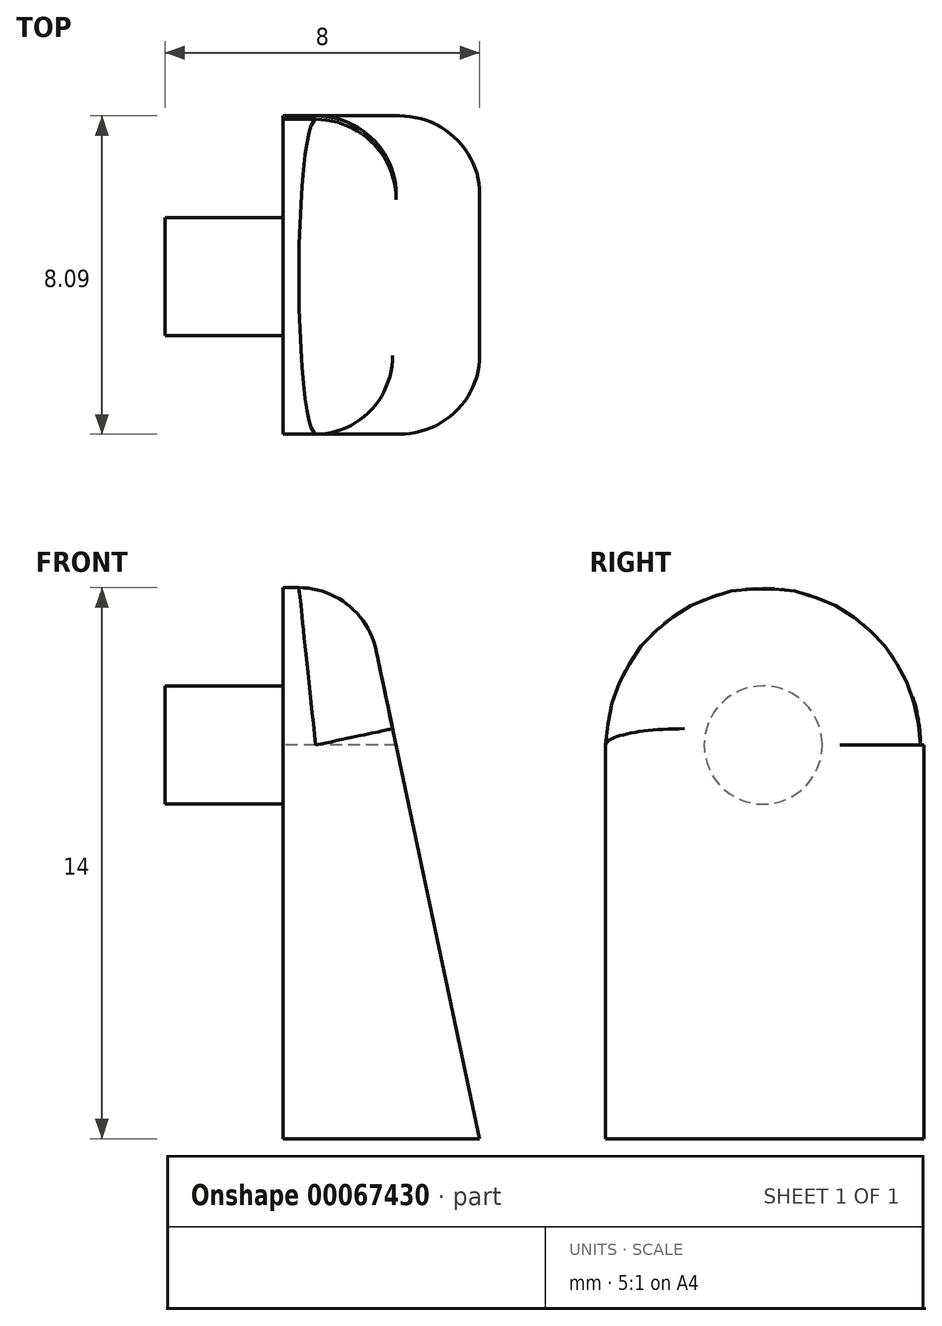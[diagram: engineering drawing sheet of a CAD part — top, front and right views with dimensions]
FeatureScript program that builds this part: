
annotation { "Feature Type Name" : "Feature", "Feature Type Description" : "" }
export const myFeature = defineFeature(function(context is Context, id is Id, definition is map)
    precondition{}
    {
        {
            var Q0;
            Q0=qCreatedBy(makeId("Right.planeOp"),FACE);
            var sketch = newSketch(context, id + "F0", { "sketchPlane" : qUnion([Q0])});
            skCircle(sketch, "E0", {"center": v(0, 0) * mm, "radius": 1.5 * mm});
            skSolve(sketch);
        }
        {
            var Q0;
            Q0 = qSketchRegion(id + "F0", true);
            extrude(context, id + "F1", {"entities" : qUnion([Q0]), "depth" : 3 * mm});
        }
        {
            var Q0;
            Q0=makeQuery(id+"F1.opExtrude","CAP_FACE",FACE,{"disambiguationData":[OSD([sQuery(id+"F0.wireOp",EDGE,"E0")])],"isStart":false});
            var sketch = newSketch(context, id + "F2", { "sketchPlane" : qUnion([Q0])});
            skArc(sketch, "E1", {"start": v(4, 0) * mm, "mid": v(0, 4) * mm, "end": v(-4, 0) * mm});
            skLineSegment(sketch, "E2.bottom", {"start": v(4, 0) * mm, "end": v(4.09, 0) * mm});
            skLineSegment(sketch, "E2.top", {"start": v(-4, -10) * mm, "end": v(4.09, -10) * mm});
            skLineSegment(sketch, "E2.left", {"start": v(-4, 0) * mm, "end": v(-4, -10) * mm});
            skLineSegment(sketch, "E2.right", {"start": v(4.09, 0) * mm, "end": v(4.09, -10) * mm});
            skLineSegment(sketch, "E3", {"start": v(4.09, -10) * mm, "end": v(0.56, -16.47) * mm, "construction": true});
            skLineSegment(sketch, "E4", {"start": v(0.56, -16.47) * mm, "end": v(-5.68, -13.07) * mm, "construction": true});
            skLineSegment(sketch, "E5", {"start": v(-5.68, -13.07) * mm, "end": v(-4, -10) * mm, "construction": true});
            skLineSegment(sketch, "E6", {"start": v(-2.56, -14.77) * mm, "end": v(-1.11, -12.12) * mm, "construction": true});
            skSolve(sketch);
        }
        {
            var Q0;
            Q0 = qSketchRegion(id + "F2", true);
            extrude(context, id + "F3", {"entities" : qUnion([Q0]), "operationType" : NewBodyOperationType.ADD, "depth" : 5 * mm});
        }
        {
            var Q0;
            Q0=makeQuery(id+"F3.opExtrude","SWEPT_FACE",FACE,{"disambiguationData":[OSD([sQuery(id+"F2.wireOp",EDGE,"E2.left")])]});
            var sketch = newSketch(context, id + "F4", { "sketchPlane" : qUnion([Q0])});
            skLineSegment(sketch, "E7", {"start": v(8, -10) * mm, "end": v(4.67, 5.66) * mm});
            skLineSegment(sketch, "E8", {"start": v(4.67, 5.66) * mm, "end": v(9.49, 5.66) * mm});
            skLineSegment(sketch, "E9", {"start": v(9.49, 5.66) * mm, "end": v(8, -10) * mm});
            skSolve(sketch);
        }
        {
            var Q0;
            Q0 = qSketchRegion(id + "F4", true);
            extrude(context, id + "F5", {"entities" : qUnion([Q0]), "operationType" : NewBodyOperationType.REMOVE, "oppositeDirection" : true, "depth" : 25 * mm});
        }
        {
            var Q0;
            Q0=makeQuery(id+"F5.boolean.opBoolean","COPY",EDGE,{"derivedFrom":makeQuery(id+"F5.opExtrude","CAP_EDGE",EDGE,{"disambiguationData":[OSD([sQuery(id+"F4.wireOp",EDGE,"E7")])],"isStart":true})});
            var Q1;
            Q1=makeQuery(id+"F5.boolean.opBoolean","INTERSECT",EDGE,{"derivedFrom":[makeQuery(id+"F3.opExtrude","SWEPT_FACE",FACE,{"disambiguationData":[OSD([sQuery(id+"F2.wireOp",EDGE,"E1")])]}),makeQuery(id+"F5.opExtrude","SWEPT_FACE",FACE,{"disambiguationData":[OSD([sQuery(id+"F4.wireOp",EDGE,"E7")])]})]});
            fillet(context, id + "F6", {"entities" : qUnion([Q0, Q1]), "radius" : 2 * mm, "tangentPropagation" : true, "allowEdgeOverflow" : false});
        }
        {
            var Q0;
            Q0=makeQuery(id+"F5.boolean.opBoolean","INTERSECT",EDGE,{"derivedFrom":[makeQuery(id+"F3.opExtrude","SWEPT_FACE",FACE,{"disambiguationData":[OSD([sQuery(id+"F2.wireOp",EDGE,"E2.right")])]}),makeQuery(id+"F5.opExtrude","SWEPT_FACE",FACE,{"disambiguationData":[OSD([sQuery(id+"F4.wireOp",EDGE,"E7")])]})]});
            fillet(context, id + "F7", {"entities" : qUnion([Q0]), "radius" : 2 * mm, "tangentPropagation" : true, "allowEdgeOverflow" : false});
        }
    });
